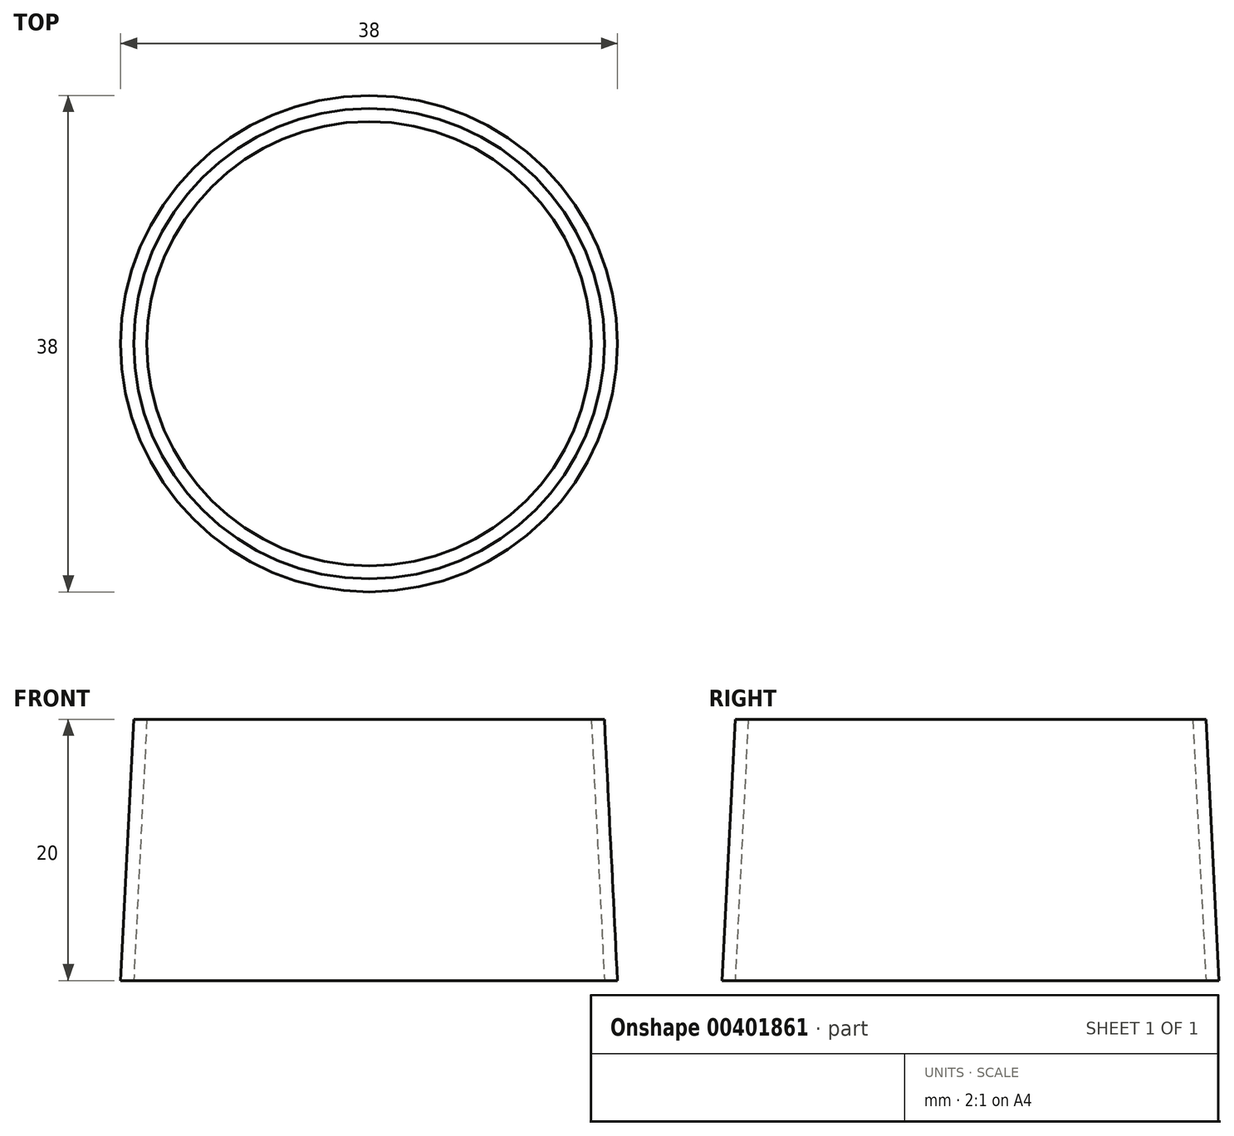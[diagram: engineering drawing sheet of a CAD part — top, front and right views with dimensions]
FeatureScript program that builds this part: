
annotation { "Feature Type Name" : "Feature", "Feature Type Description" : "" }
export const myFeature = defineFeature(function(context is Context, id is Id, definition is map)
    precondition{}
    {
        {
            var Q0;
            Q0=qCreatedBy(makeId("Front.planeOp"),FACE);
            var sketch = newSketch(context, id + "F0", { "sketchPlane" : qUnion([Q0])});
            skLineSegment(sketch, "E0", {"start": v(-18, 0) * mm, "end": v(-17, 20) * mm});
            skLineSegment(sketch, "E1", {"start": v(-17, 20) * mm, "end": v(-18, 20) * mm});
            skLineSegment(sketch, "E2", {"start": v(-18, 20) * mm, "end": v(-19, 0) * mm});
            skLineSegment(sketch, "E3", {"start": v(-19, 0) * mm, "end": v(-18, 0) * mm});
            skLineSegment(sketch, "E4", {"start": v(0, 56.65) * mm, "end": v(0, -58.75) * mm, "construction": true});
            skSolve(sketch);
        }
        {
            var Q0;
            Q0=makeQuery(id+"F0.imprint","IMPRINT",FACE,{"disambiguationData":[TD([[makeQuery(id+"F0.imprint","IMPRINT",EDGE,{"derivedFrom":sQuery(id+"F0.wireOp",EDGE,"E0")}),1.0]])]});
            var Q1;
            Q1=sQuery(id+"F0.wireOp",EDGE,"E4");
            revolve(context, id + "F1", {"surfaceOperationType" : NewSurfaceOperationType.NEW, "entities" : qUnion([Q0]), "axis" : qUnion([Q1]), "revolveType" : RevolveType.FULL});
        }
    });
